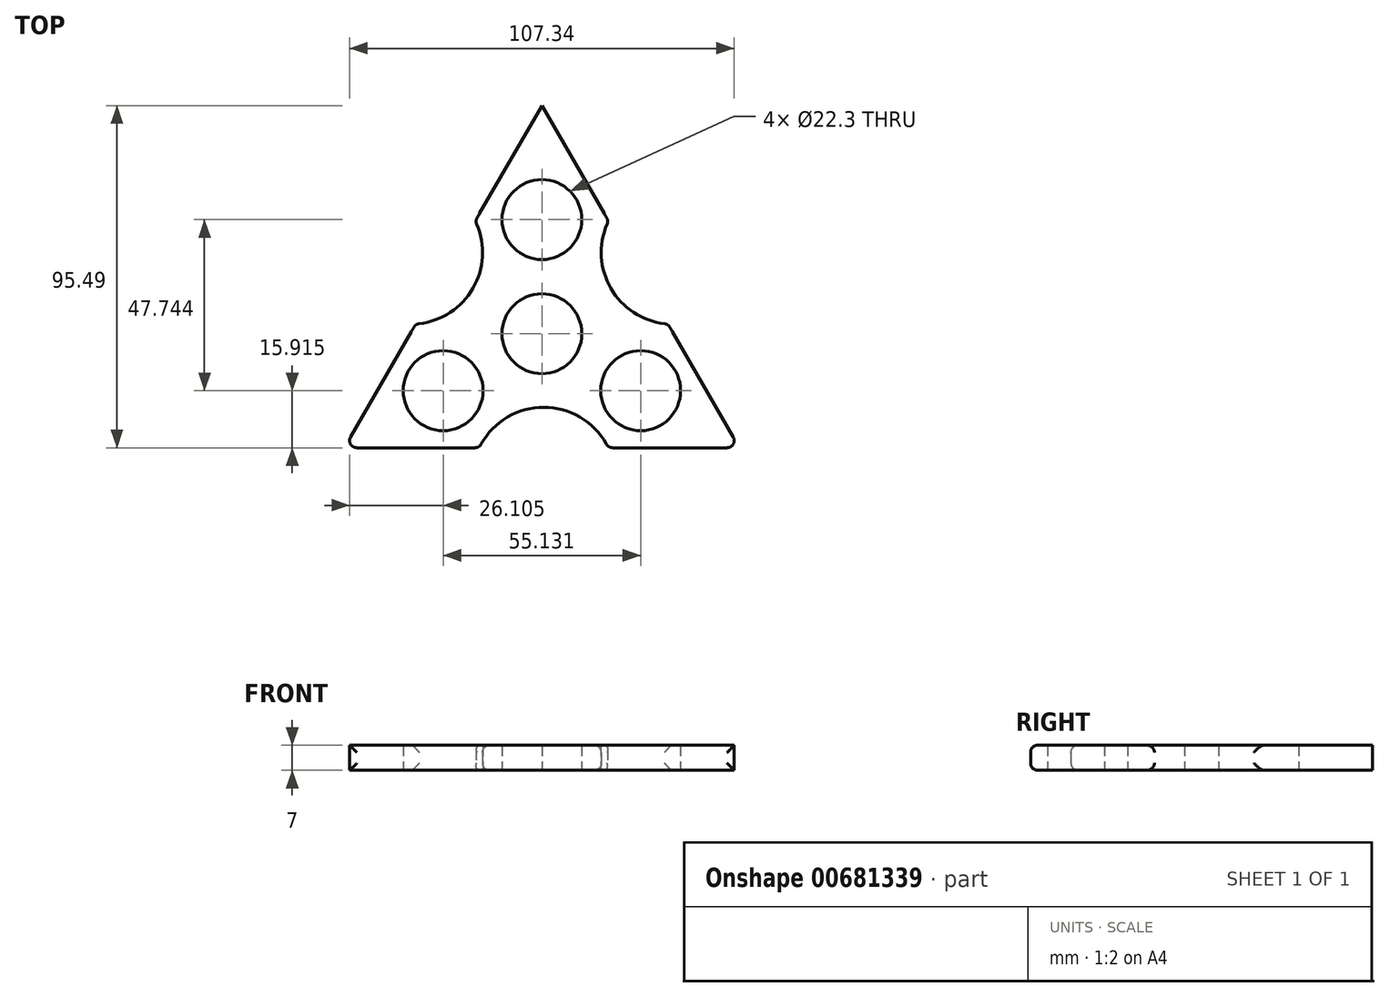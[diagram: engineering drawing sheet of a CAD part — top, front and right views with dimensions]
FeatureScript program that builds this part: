
annotation { "Feature Type Name" : "Feature", "Feature Type Description" : "" }
export const myFeature = defineFeature(function(context is Context, id is Id, definition is map)
    precondition{}
    {
        {
            var Q0;
            Q0=qCreatedBy(makeId("Top.planeOp"),FACE);
            var sketch = newSketch(context, id + "F0", { "sketchPlane" : qUnion([Q0])});
            skCircle(sketch, "E0", {"center": v(0, 0) * mm, "radius": 11.15 * mm});
            skCircle(sketch, "E1.cCircle", {"center": v(0, 0) * mm, "radius": 31.83 * mm, "construction": true});
            skLineSegment(sketch, "E1.0", {"start": v(0, 63.66) * mm, "end": v(55.13, -31.83) * mm});
            skLineSegment(sketch, "E1.1", {"start": v(55.13, -31.83) * mm, "end": v(-55.13, -31.83) * mm});
            skLineSegment(sketch, "E1.2", {"start": v(-55.13, -31.83) * mm, "end": v(0, 63.66) * mm});
            skPoint(sketch, "E1.0.midPoint", {"position": v(27.57, 15.91) * mm});
            skCircle(sketch, "E2", {"center": v(0, 31.83) * mm, "radius": 11.15 * mm});
            skCircle(sketch, "E3", {"center": v(-27.57, -15.91) * mm, "radius": 11.15 * mm});
            skCircle(sketch, "E4", {"center": v(27.57, -15.91) * mm, "radius": 11.15 * mm});
            skArc(sketch, "E5", {"start": v(18.6, 31.43) * mm, "mid": v(19.25, 12.65) * mm, "end": v(35.2, 2.7) * mm});
            skArc(sketch, "E6", {"start": v(-35.2, 2.7) * mm, "mid": v(-19.25, 12.65) * mm, "end": v(-18.6, 31.43) * mm});
            skArc(sketch, "E7", {"start": v(18.52, -31.83) * mm, "mid": v(0.52, -20.55) * mm, "end": v(-17.48, -31.83) * mm});
            skSolve(sketch);
        }
        {
            var Q0;
            {var subQ3=sQuery(id+"F0.wireOp",EDGE,"E5");Q0=makeQuery(id+"F0.imprint","IMPRINT",FACE,{"disambiguationData":[TD([[makeQuery(id+"F0.imprint","IMPRINT",EDGE,{"derivedFrom":subQ3}),-1.0]])]});}
            var Q1;
            {var subQ8=sQuery(id+"F0.wireOp",EDGE,"E6");Q1=makeQuery(id+"F0.imprint","IMPRINT",FACE,{"disambiguationData":[TD([[makeQuery(id+"F0.imprint","IMPRINT",EDGE,{"derivedFrom":subQ8}),-1.0]])]});}
            var Q2;
            {var subQ7=sQuery(id+"F0.wireOp",EDGE,"xMdd2QT4-DnYW-gvGh-Ep5M-rRxMcIko8WzS");Q2=makeQuery(id+"F0.imprint","IMPRINT",FACE,{"disambiguationData":[TD([[makeQuery(id+"F0.imprint","IMPRINT",EDGE,{"derivedFrom":subQ7}),-1.0]])]});}
            extrude(context, id + "F1", {"entities" : qUnion([Q0, Q1, Q2]), "depth" : 7 * mm, "offsetDistance" : 25 * mm});
        }
        {
            var Q0;
            {var subQ0=sQuery(id+"F0.wireOp",EDGE,"E1.1");Q0=makeQuery(id+"F1.opExtrude","SWEPT_FACE",FACE,{"disambiguationData":[OSD([subQ0]),TDD([makeQuery(id+"F0.imprint","IMPRINT",EDGE,{"disambiguationData":[TD([[makeQuery(id+"F0.imprint","INTERSECT",VERTEX,{"disambiguationData":[OD(0.0)],"derivedFrom":[subQ0,sQuery(id+"F0.wireOp",EDGE,"xMdd2QT4-DnYW-gvGh-Ep5M-rRxMcIko8WzS")]}),1.0]])],"derivedFrom":subQ0})])]});}
            var Q1;
            Q1=makeQuery(id+"F1.opExtrude","SWEPT_FACE",FACE,{"disambiguationData":[OSD([sQuery(id+"F0.wireOp",EDGE,"xMdd2QT4-DnYW-gvGh-Ep5M-rRxMcIko8WzS")])]});
            var Q2;
            {var subQ0=sQuery(id+"F0.wireOp",EDGE,"E1.1");Q2=makeQuery(id+"F1.opExtrude","SWEPT_FACE",FACE,{"disambiguationData":[OSD([subQ0]),TDD([makeQuery(id+"F0.imprint","IMPRINT",EDGE,{"disambiguationData":[TD([[makeQuery(id+"F0.imprint","INTERSECT",VERTEX,{"disambiguationData":[OD(1.0)],"derivedFrom":[subQ0,sQuery(id+"F0.wireOp",EDGE,"xMdd2QT4-DnYW-gvGh-Ep5M-rRxMcIko8WzS")]}),-1.0]])],"derivedFrom":subQ0})])]});}
            var Q3;
            {var subQ0=sQuery(id+"F0.wireOp",EDGE,"E1.0");Q3=makeQuery(id+"F1.opExtrude","SWEPT_FACE",FACE,{"disambiguationData":[OSD([subQ0]),TDD([makeQuery(id+"F0.imprint","IMPRINT",EDGE,{"disambiguationData":[TD([[makeQuery(id+"F0.imprint","INTERSECT",VERTEX,{"disambiguationData":[OD(1.0)],"derivedFrom":[subQ0,sQuery(id+"F0.wireOp",EDGE,"E5")]}),-1.0]])],"derivedFrom":subQ0})])]});}
            var Q4;
            Q4=makeQuery(id+"F1.opExtrude","SWEPT_FACE",FACE,{"disambiguationData":[OSD([sQuery(id+"F0.wireOp",EDGE,"E5")])]});
            var Q5;
            {var subQ0=sQuery(id+"F0.wireOp",EDGE,"E1.0");Q5=makeQuery(id+"F1.opExtrude","SWEPT_FACE",FACE,{"disambiguationData":[OSD([subQ0]),TDD([makeQuery(id+"F0.imprint","IMPRINT",EDGE,{"disambiguationData":[TD([[makeQuery(id+"F0.imprint","INTERSECT",VERTEX,{"disambiguationData":[OD(0.0)],"derivedFrom":[subQ0,sQuery(id+"F0.wireOp",EDGE,"E5")]}),1.0]])],"derivedFrom":subQ0})])]});}
            var Q6;
            {var subQ0=sQuery(id+"F0.wireOp",EDGE,"E1.2");Q6=makeQuery(id+"F1.opExtrude","SWEPT_FACE",FACE,{"disambiguationData":[OSD([subQ0]),TDD([makeQuery(id+"F0.imprint","IMPRINT",EDGE,{"disambiguationData":[TD([[makeQuery(id+"F0.imprint","INTERSECT",VERTEX,{"disambiguationData":[OD(1.0)],"derivedFrom":[subQ0,sQuery(id+"F0.wireOp",EDGE,"E6")]}),-1.0]])],"derivedFrom":subQ0})])]});}
            var Q7;
            Q7=makeQuery(id+"F1.opExtrude","SWEPT_FACE",FACE,{"disambiguationData":[OSD([sQuery(id+"F0.wireOp",EDGE,"E6")])]});
            var Q8;
            {var subQ0=sQuery(id+"F0.wireOp",EDGE,"E1.2");Q8=makeQuery(id+"F1.opExtrude","SWEPT_FACE",FACE,{"disambiguationData":[OSD([subQ0]),TDD([makeQuery(id+"F0.imprint","IMPRINT",EDGE,{"disambiguationData":[TD([[makeQuery(id+"F0.imprint","INTERSECT",VERTEX,{"disambiguationData":[OD(0.0)],"derivedFrom":[subQ0,sQuery(id+"F0.wireOp",EDGE,"E6")]}),1.0]])],"derivedFrom":subQ0})])]});}
            var Q9;
            Q9=makeQuery(id+"F1.opExtrude","SWEPT_FACE",FACE,{"disambiguationData":[OSD([sQuery(id+"F0.wireOp",EDGE,"E7")])]});
            var Q10;
            {var subQ0=sQuery(id+"F0.wireOp",EDGE,"E1.1");Q10=makeQuery(id+"F1.opExtrude","SWEPT_FACE",FACE,{"disambiguationData":[OSD([subQ0]),TDD([makeQuery(id+"F0.imprint","IMPRINT",EDGE,{"disambiguationData":[TD([[makeQuery(id+"F0.imprint","INTERSECT",VERTEX,{"derivedFrom":[subQ0,sQuery(id+"F0.wireOp",EDGE,"E1.2")]}),1.0]])],"derivedFrom":subQ0})])]});}
            var Q11;
            {var subQ0=sQuery(id+"F0.wireOp",EDGE,"E1.1");Q11=makeQuery(id+"F1.opExtrude","SWEPT_FACE",FACE,{"disambiguationData":[OSD([subQ0]),TDD([makeQuery(id+"F0.imprint","IMPRINT",EDGE,{"disambiguationData":[TD([[makeQuery(id+"F0.imprint","INTERSECT",VERTEX,{"derivedFrom":[sQuery(id+"F0.wireOp",EDGE,"E1.0"),subQ0]}),-1.0]])],"derivedFrom":subQ0})])]});}
            fillet(context, id + "F2", {"entities" : qUnion([Q0, Q1, Q2, Q3, Q4, Q5, Q6, Q7, Q8, Q9, Q10, Q11]), "radius" : 2 * mm, "tangentPropagation" : true, "allowEdgeOverflow" : false});
        }
    });
